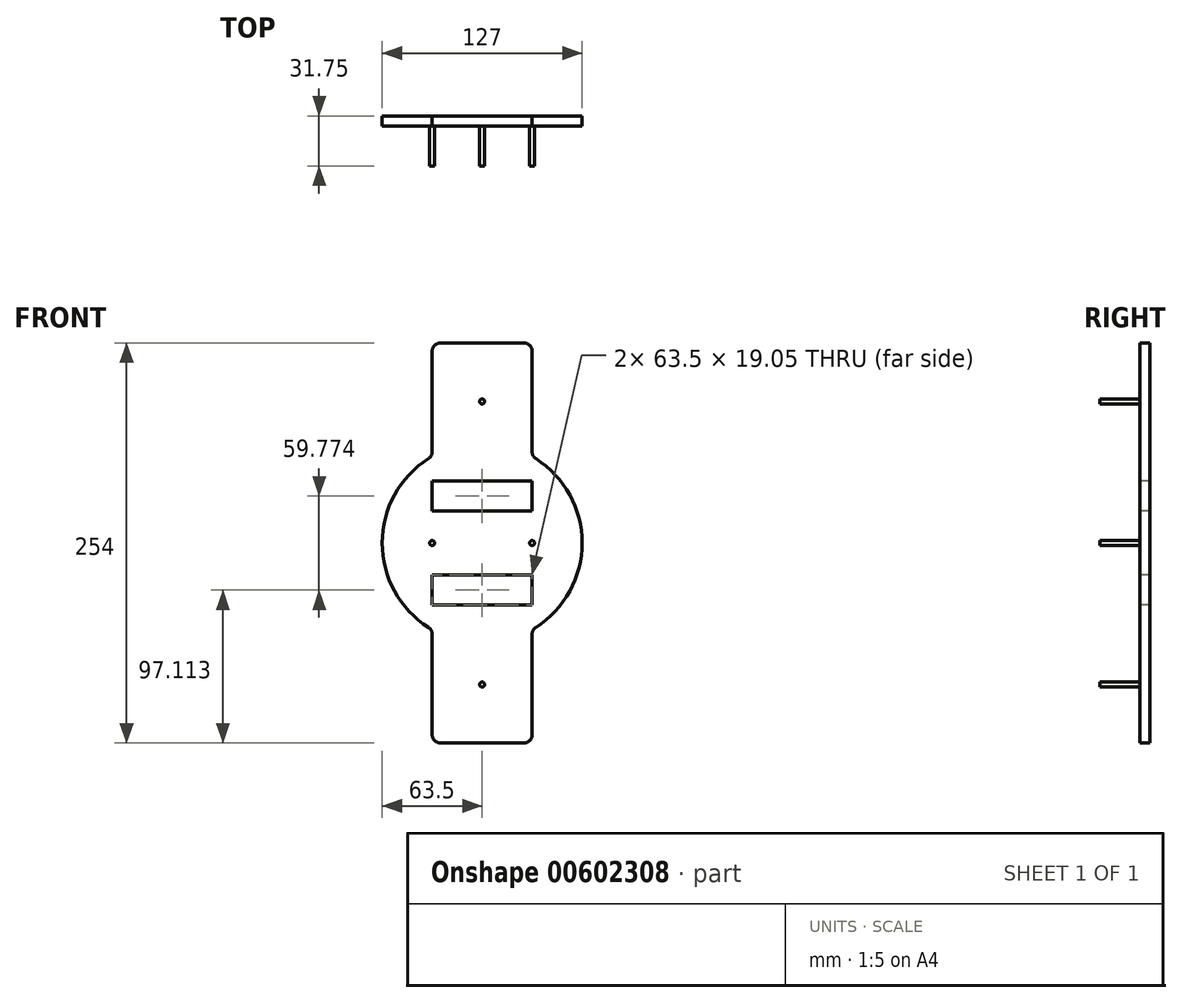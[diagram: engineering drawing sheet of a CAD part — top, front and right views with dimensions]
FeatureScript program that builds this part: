
annotation { "Feature Type Name" : "Feature", "Feature Type Description" : "" }
export const myFeature = defineFeature(function(context is Context, id is Id, definition is map)
    precondition{}
    {
        {
            var Q0;
            Q0=qCreatedBy(makeId("Front.planeOp"),FACE);
            var sketch = newSketch(context, id + "F0", { "sketchPlane" : qUnion([Q0])});
            skCircle(sketch, "E0", {"center": v(0, 0) * mm, "radius": 63.5 * mm});
            skLineSegment(sketch, "E1.bottom", {"start": v(-31.75, 127) * mm, "end": v(31.75, 127) * mm});
            skLineSegment(sketch, "E1.top", {"start": v(-31.75, -127) * mm, "end": v(31.75, -127) * mm});
            skLineSegment(sketch, "E1.left", {"start": v(-31.75, 127) * mm, "end": v(-31.75, -127) * mm});
            skLineSegment(sketch, "E1.right", {"start": v(31.75, 127) * mm, "end": v(31.75, -127) * mm});
            skSolve(sketch);
        }
        {
            var Q0;
            Q0=qSketchRegion(id+"F0",true);
            extrude(context, id + "F1", {"entities" : qUnion([Q0]), "depth" : 6.35 * mm});
        }
        {
            var Q0;
            {var subQ0=sQuery(id+"F0.wireOp",EDGE,"E1.right");var subQ1=sQuery(id+"F0.wireOp",EDGE,"E0");Q0=makeQuery(id+"F1.opExtrude","SWEPT_EDGE",EDGE,{"disambiguationData":[OSD([subQ1,subQ0]),TDD([makeQuery(id+"F0.imprint","INTERSECT",VERTEX,{"disambiguationData":[OD(0.0)],"derivedFrom":[subQ1,subQ0]})])]});}
            var Q1;
            {var subQ0=sQuery(id+"F0.wireOp",EDGE,"E1.left");var subQ1=sQuery(id+"F0.wireOp",EDGE,"E0");Q1=makeQuery(id+"F1.opExtrude","SWEPT_EDGE",EDGE,{"disambiguationData":[OSD([subQ1,subQ0]),TDD([makeQuery(id+"F0.imprint","INTERSECT",VERTEX,{"disambiguationData":[OD(0.0)],"derivedFrom":[subQ1,subQ0]})])]});}
            var Q2;
            {var subQ0=sQuery(id+"F0.wireOp",EDGE,"E1.left");var subQ1=sQuery(id+"F0.wireOp",EDGE,"E0");Q2=makeQuery(id+"F1.opExtrude","SWEPT_EDGE",EDGE,{"disambiguationData":[OSD([subQ1,subQ0]),TDD([makeQuery(id+"F0.imprint","INTERSECT",VERTEX,{"disambiguationData":[OD(1.0)],"derivedFrom":[subQ1,subQ0]})])]});}
            var Q3;
            {var subQ0=sQuery(id+"F0.wireOp",EDGE,"E1.right");var subQ1=sQuery(id+"F0.wireOp",EDGE,"E0");Q3=makeQuery(id+"F1.opExtrude","SWEPT_EDGE",EDGE,{"disambiguationData":[OSD([subQ1,subQ0]),TDD([makeQuery(id+"F0.imprint","INTERSECT",VERTEX,{"disambiguationData":[OD(1.0)],"derivedFrom":[subQ1,subQ0]})])]});}
            var Q4;
            Q4=makeQuery(id+"F1.opExtrude","SWEPT_EDGE",EDGE,{"disambiguationData":[OSD([sQuery(id+"F0.wireOp",EDGE,"E1.bottom"),sQuery(id+"F0.wireOp",EDGE,"E1.right")])]});
            var Q5;
            Q5=makeQuery(id+"F1.opExtrude","SWEPT_EDGE",EDGE,{"disambiguationData":[OSD([sQuery(id+"F0.wireOp",EDGE,"E1.bottom"),sQuery(id+"F0.wireOp",EDGE,"E1.left")])]});
            var Q6;
            Q6=makeQuery(id+"F1.opExtrude","SWEPT_EDGE",EDGE,{"disambiguationData":[OSD([sQuery(id+"F0.wireOp",EDGE,"E1.top"),sQuery(id+"F0.wireOp",EDGE,"E1.right")])]});
            var Q7;
            Q7=makeQuery(id+"F1.opExtrude","SWEPT_EDGE",EDGE,{"disambiguationData":[OSD([sQuery(id+"F0.wireOp",EDGE,"E1.top"),sQuery(id+"F0.wireOp",EDGE,"E1.left")])]});
            fillet(context, id + "F2", {"entities" : qUnion([Q0, Q1, Q2, Q3, Q4, Q5, Q6, Q7]), "radius" : 5.08 * mm, "tangentPropagation" : true, "allowEdgeOverflow" : false});
        }
        {
            var Q0;
            Q0=makeQuery(id+"F1.opExtrude","CAP_FACE",FACE,{"disambiguationData":[OSD([sQuery(id+"F0.wireOp",EDGE,"E0"),sQuery(id+"F0.wireOp",EDGE,"E1.bottom"),sQuery(id+"F0.wireOp",EDGE,"E1.top"),sQuery(id+"F0.wireOp",EDGE,"E1.left"),sQuery(id+"F0.wireOp",EDGE,"E1.right")])],"isStart":false});
            var sketch = newSketch(context, id + "F3", { "sketchPlane" : qUnion([Q0])});
            skLineSegment(sketch, "E2", {"start": v(-31.75, 39.41) * mm, "end": v(-31.75, 20.36) * mm});
            skLineSegment(sketch, "E3", {"start": v(-31.75, 20.36) * mm, "end": v(31.75, 20.36) * mm});
            skLineSegment(sketch, "E4", {"start": v(31.75, 20.36) * mm, "end": v(31.75, 39.41) * mm});
            skLineSegment(sketch, "E5", {"start": v(31.75, 39.41) * mm, "end": v(-31.75, 39.41) * mm});
            skLineSegment(sketch, "E6", {"start": v(-63.5, 0) * mm, "end": v(63.5, 0) * mm, "construction": true});
            skLineSegment(sketch, "E7.MirrorCS", {"start": v(-31.75, -20.36) * mm, "end": v(31.75, -20.36) * mm});
            skLineSegment(sketch, "E8.MirrorCS", {"start": v(-31.75, -39.41) * mm, "end": v(-31.75, -20.36) * mm});
            skLineSegment(sketch, "E9.MirrorCS", {"start": v(31.75, -39.41) * mm, "end": v(-31.75, -39.41) * mm});
            skLineSegment(sketch, "E10.MirrorCS", {"start": v(31.75, -20.36) * mm, "end": v(31.75, -39.41) * mm});
            skSolve(sketch);
        }
        {
            var Q0;
            Q0=makeQuery(id+"F3.imprint","IMPRINT",FACE,{"disambiguationData":[TD([[makeQuery(id+"F3.imprint","IMPRINT",EDGE,{"derivedFrom":sQuery(id+"F3.wireOp",EDGE,"E2")}),1.0]])]});
            var Q1;
            Q1=makeQuery(id+"F3.imprint","IMPRINT",FACE,{"disambiguationData":[TD([[makeQuery(id+"F3.imprint","IMPRINT",EDGE,{"derivedFrom":sQuery(id+"F3.wireOp",EDGE,"E7.MirrorCS")}),-1.0]])]});
            extrude(context, id + "F4", {"entities" : qUnion([Q0, Q1]), "operationType" : NewBodyOperationType.REMOVE, "oppositeDirection" : true, "depth" : 25.4 * mm});
        }
        {
            var Q0;
            Q0=makeQuery(id+"F1.opExtrude","CAP_FACE",FACE,{"disambiguationData":[OSD([sQuery(id+"F0.wireOp",EDGE,"E0"),sQuery(id+"F0.wireOp",EDGE,"E1.bottom"),sQuery(id+"F0.wireOp",EDGE,"E1.top"),sQuery(id+"F0.wireOp",EDGE,"E1.left"),sQuery(id+"F0.wireOp",EDGE,"E1.right")])],"isStart":false});
            var sketch = newSketch(context, id + "F5", { "sketchPlane" : qUnion([Q0])});
            skCircle(sketch, "E11", {"center": v(-31.75, 0) * mm, "radius": 1.59 * mm});
            skCircle(sketch, "E12", {"center": v(31.75, 0) * mm, "radius": 1.59 * mm});
            skCircle(sketch, "E13", {"center": v(0, -89.89) * mm, "radius": 1.59 * mm});
            skPoint(sketch, "E13.centerSnap0", {"position": v(-31.75, -89.89) * mm});
            skCircle(sketch, "E14", {"center": v(0, 89.89) * mm, "radius": 1.59 * mm});
            skPoint(sketch, "E14.centerSnap0", {"position": v(-31.75, 89.89) * mm});
            skSolve(sketch);
        }
        {
            var Q0;
            Q0=qSketchRegion(id+"F5",true);
            extrude(context, id + "F6", {"entities" : qUnion([Q0]), "operationType" : NewBodyOperationType.ADD, "depth" : 25.4 * mm});
        }
    });
